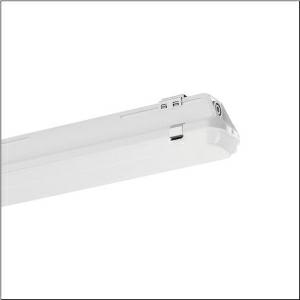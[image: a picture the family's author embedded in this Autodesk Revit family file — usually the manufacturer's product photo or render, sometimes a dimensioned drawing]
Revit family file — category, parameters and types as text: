
# Revit family: monsun_r__12_51fp20tp960x_0314
name_source: partatom
category: Lighting Fixtures
units: mm (PartAtom-declared; Revit-internal decimal feet)

## family parameters
Cut with Voids When Loaded = No
Host = Face
Light Source = No
Part Type = Normal
Room Calculation Point = No
Round Connector Dimension = Use Diameter
Shared = No

## types (1)
- --- (1 x LED 2700 K ... 6500 K, 5420 lm, 36.8 W, 6500K)
    Apparent Load = 37 VA
    CIE Flux Codes = 45 75 93 94 100
    Color Rendering = 80
    Color Temperature = 6500K
    Default Elevation = 1800 mm
    Description = Monsun® 12, damp-proof luminaire, chain hanger, primary optical cover: enclosure, of PC, light emission: direct distribution, primary light characteristic: symmetric, installation type: suspended mounting, surface-mounted, horizontal mounting, vertical mounting, LED rated luminous flux: 5.410 lm, light colour: 8tw, colour temperature: 2700..6500K, control gear: ECG DALI, with terminal, 5-pole, max. 2.5mm², mains connection: 220..240V, AC, 50/60Hz, rated input power: 37W, luminaire housing, of glass-fibre reinforced polyester, uncoated, bright grey, length: 1.590 mm, width: 90 mm, height: 88mm, clip for enclosure, of stainless steel (V2A), ceiling mounting element, of stainless steel (V2A), chain hanger, of stainless steel (V2A), protection rating (complete): IP66, insulation class (complete): insulation class I (protective earthing), certification: CE, ENEC, VDE, protection symbol: D, impact resistance: IK08, permissible ambient temperature for indoor applications: -25..+35°C, standard: EN 50419, EN 60598-2-1, no direct snow, no direct sun, no direct rain, for indoor or canopied outdoor use, corresponds to IFS (International Featured Standards) requirements for safety and quality in the food industry, packaging unit: 1 piece
    Height = 89 mm
    Lamp = 1 x LED 2700 K ... 6500 K
    Lamp Light Flux = 5420 lm
    Lamp Power = 36.8 W
    Lamp count = 1
    Length = 1590 mm
    Luminous efficacy = 147 lm/W
    Manufacturer = Siteco
    ModVariant = No
    Model = 51FP20TP960X
    Mounting Place = Ceiling
    Mounting Type = Pendant
    Number of Poles = 1
    OnlyDefault = Yes
    Power Factor = 1
    Product Name = Monsun® 12
    Product group = damp-proof luminaire | ceiling pendant
    ProductGroupID = 908
    Protection Class = Protection class I
    Protection Degree = IP 66
    RLX_Detail_Level = 1
    RlxData = <blob elided: 88553 chars, md5=4f88f991>
    Socket = socket
    Standby Power = 0 W
    System Light Flux = 5420 lm
    System Power = 37 W
    Type Comments = individual setting: CCT=6500K
    Type Image = l_1004748.jpg
    URL = http://relux.com
    VarID = @adj_133877
    Voltage = 0 V
    Weight = 0.00 kg
    Width = 90 mm

## geometry (parser evidence)
native form markers: Blend x4, Sweep x14
no freeform markers — native parametric forms only
